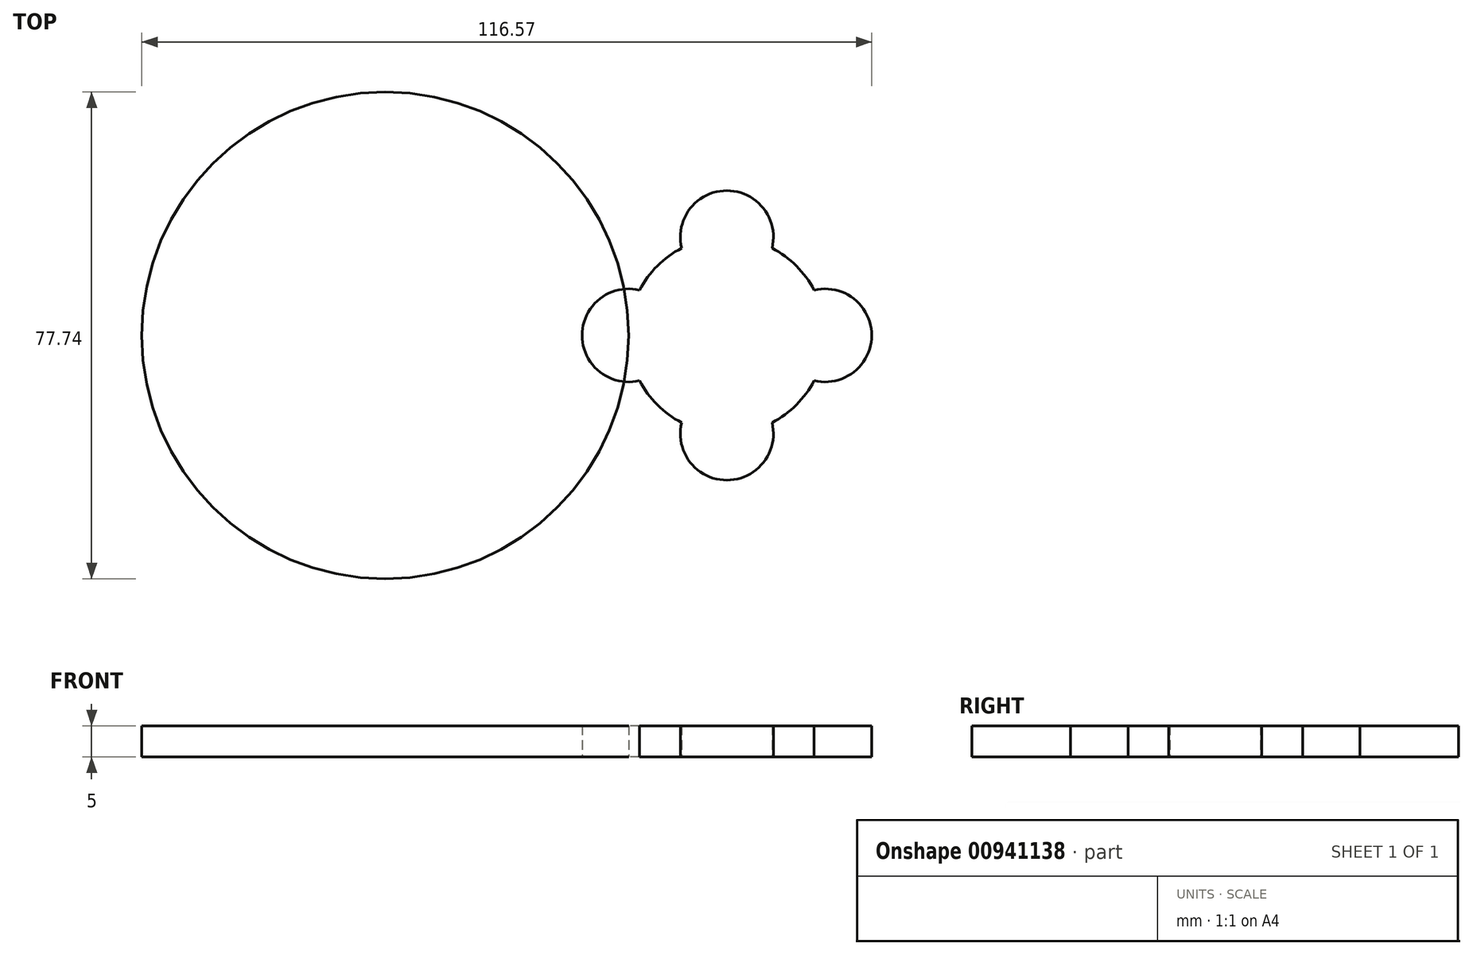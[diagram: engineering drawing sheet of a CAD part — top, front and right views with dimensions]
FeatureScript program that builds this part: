
annotation { "Feature Type Name" : "Feature", "Feature Type Description" : "" }
export const myFeature = defineFeature(function(context is Context, id is Id, definition is map)
    precondition{}
    {
        {
            var Q0;
            Q0=qCreatedBy(makeId("Top.planeOp"),FACE);
            var sketch = newSketch(context, id + "F0", { "sketchPlane" : qUnion([Q0])});
            skCircle(sketch, "E0", {"center": v(0, 0) * mm, "radius": 38.87 * mm});
            skSolve(sketch);
        }
        {
            var Q0;
            Q0=qCreatedBy(makeId("Top.planeOp"),FACE);
            var sketch = newSketch(context, id + "F1", { "sketchPlane" : qUnion([Q0])});
            skCircle(sketch, "E1", {"center": v(54.57, 0) * mm, "radius": 15.7 * mm});
            skCircle(sketch, "E2", {"center": v(38.87, 0) * mm, "radius": 7.43 * mm});
            skCircle(sketch, "E3", {"center": v(54.57, 15.7) * mm, "radius": 7.43 * mm});
            skCircle(sketch, "E4", {"center": v(70.27, 0) * mm, "radius": 7.43 * mm});
            skCircle(sketch, "E5", {"center": v(54.57, -15.7) * mm, "radius": 7.43 * mm});
            skSolve(sketch);
        }
        {
            var Q0;
            Q0=makeQuery(id+"F0.imprint","IMPRINT",FACE,{"disambiguationData":[TD([[makeQuery(id+"F0.imprint","IMPRINT",EDGE,{"derivedFrom":sQuery(id+"F0.wireOp",EDGE,"E0")}),1.0]])]});
            extrude(context, id + "F2", {"entities" : qUnion([Q0]), "depth" : 5 * mm, "offsetDistance" : 25 * mm});
        }
        {
            var Q0;
            {var subQ0=sQuery(id+"F1.wireOp",EDGE,"E3");var subQ1=sQuery(id+"F1.wireOp",EDGE,"E1");var subQ2=makeQuery(id+"F1.imprint","INTERSECT",VERTEX,{"disambiguationData":[OD(0.0)],"derivedFrom":[subQ1,subQ0]});Q0=makeQuery(id+"F1.imprint","IMPRINT",FACE,{"disambiguationData":[TD([[makeQuery(id+"F1.imprint","IMPRINT",EDGE,{"disambiguationData":[TD([[subQ2,-1.0]])],"derivedFrom":subQ1}),-1.0]])]});}
            var Q1;
            {var subQ0=sQuery(id+"F1.wireOp",EDGE,"E2");var subQ1=sQuery(id+"F1.wireOp",EDGE,"E1");var subQ2=makeQuery(id+"F1.imprint","INTERSECT",VERTEX,{"disambiguationData":[OD(0.0)],"derivedFrom":[subQ1,subQ0]});Q1=makeQuery(id+"F1.imprint","IMPRINT",FACE,{"disambiguationData":[TD([[makeQuery(id+"F1.imprint","IMPRINT",EDGE,{"disambiguationData":[TD([[subQ2,-1.0]])],"derivedFrom":subQ1}),-1.0]])]});}
            var Q2;
            {var subQ0=sQuery(id+"F1.wireOp",EDGE,"E2");var subQ1=sQuery(id+"F1.wireOp",EDGE,"E1");var subQ2=makeQuery(id+"F1.imprint","INTERSECT",VERTEX,{"disambiguationData":[OD(0.0)],"derivedFrom":[subQ1,subQ0]});Q2=makeQuery(id+"F1.imprint","IMPRINT",FACE,{"disambiguationData":[TD([[makeQuery(id+"F1.imprint","IMPRINT",EDGE,{"disambiguationData":[TD([[subQ2,-1.0]])],"derivedFrom":subQ1}),1.0]])]});}
            var Q3;
            {var subQ0=sQuery(id+"F1.wireOp",EDGE,"E3");var subQ1=sQuery(id+"F1.wireOp",EDGE,"E1");var subQ2=makeQuery(id+"F1.imprint","INTERSECT",VERTEX,{"disambiguationData":[OD(0.0)],"derivedFrom":[subQ1,subQ0]});Q3=makeQuery(id+"F1.imprint","IMPRINT",FACE,{"disambiguationData":[TD([[makeQuery(id+"F1.imprint","IMPRINT",EDGE,{"disambiguationData":[TD([[subQ2,-1.0]])],"derivedFrom":subQ1}),1.0]])]});}
            var Q4;
            {var subQ0=sQuery(id+"F1.wireOp",EDGE,"E4");var subQ1=sQuery(id+"F1.wireOp",EDGE,"E1");var subQ2=makeQuery(id+"F1.imprint","INTERSECT",VERTEX,{"disambiguationData":[OD(0.0)],"derivedFrom":[subQ1,subQ0]});Q4=makeQuery(id+"F1.imprint","IMPRINT",FACE,{"disambiguationData":[TD([[makeQuery(id+"F1.imprint","IMPRINT",EDGE,{"disambiguationData":[TD([[subQ2,1.0]])],"derivedFrom":subQ1}),1.0]])]});}
            var Q5;
            {var subQ0=sQuery(id+"F1.wireOp",EDGE,"E4");var subQ1=sQuery(id+"F1.wireOp",EDGE,"E1");var subQ2=makeQuery(id+"F1.imprint","INTERSECT",VERTEX,{"disambiguationData":[OD(0.0)],"derivedFrom":[subQ1,subQ0]});Q5=makeQuery(id+"F1.imprint","IMPRINT",FACE,{"disambiguationData":[TD([[makeQuery(id+"F1.imprint","IMPRINT",EDGE,{"disambiguationData":[TD([[subQ2,1.0]])],"derivedFrom":subQ1}),-1.0]])]});}
            var Q6;
            {var subQ0=sQuery(id+"F1.wireOp",EDGE,"E5");var subQ1=sQuery(id+"F1.wireOp",EDGE,"E1");var subQ2=makeQuery(id+"F1.imprint","INTERSECT",VERTEX,{"disambiguationData":[OD(0.0)],"derivedFrom":[subQ1,subQ0]});Q6=makeQuery(id+"F1.imprint","IMPRINT",FACE,{"disambiguationData":[TD([[makeQuery(id+"F1.imprint","IMPRINT",EDGE,{"disambiguationData":[TD([[subQ2,-1.0]])],"derivedFrom":subQ1}),-1.0]])]});}
            var Q7;
            {var subQ0=sQuery(id+"F1.wireOp",EDGE,"E5");var subQ1=sQuery(id+"F1.wireOp",EDGE,"E1");var subQ2=makeQuery(id+"F1.imprint","INTERSECT",VERTEX,{"disambiguationData":[OD(0.0)],"derivedFrom":[subQ1,subQ0]});Q7=makeQuery(id+"F1.imprint","IMPRINT",FACE,{"disambiguationData":[TD([[makeQuery(id+"F1.imprint","IMPRINT",EDGE,{"disambiguationData":[TD([[subQ2,-1.0]])],"derivedFrom":subQ1}),1.0]])]});}
            var Q8;
            {var subQ1=sQuery(id+"F1.wireOp",EDGE,"E1");var subQ8=sQuery(id+"F1.wireOp",EDGE,"E3");var subQ11=makeQuery(id+"F1.imprint","INTERSECT",VERTEX,{"disambiguationData":[OD(0.0)],"derivedFrom":[subQ1,subQ8]});Q8=makeQuery(id+"F1.imprint","IMPRINT",FACE,{"disambiguationData":[TD([[makeQuery(id+"F1.imprint","IMPRINT",EDGE,{"disambiguationData":[TD([[subQ11,1.0]])],"derivedFrom":subQ1}),1.0]])]});}
            extrude(context, id + "F3", {"entities" : qUnion([Q0, Q1, Q2, Q3, Q4, Q5, Q6, Q7, Q8]), "depth" : 5 * mm, "offsetDistance" : 25 * mm});
        }
    });
